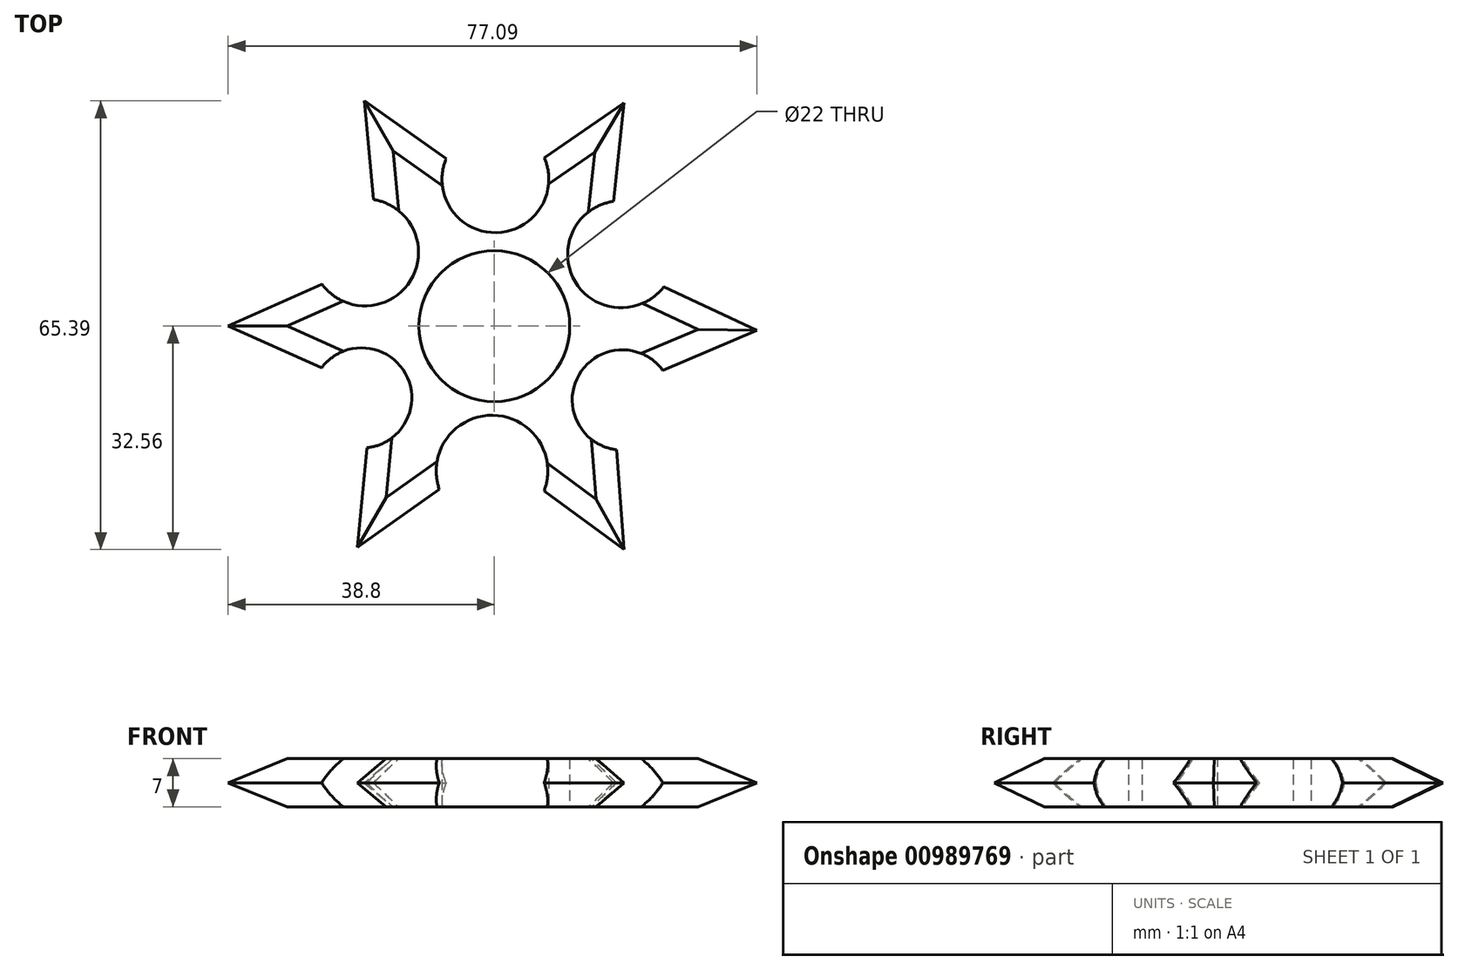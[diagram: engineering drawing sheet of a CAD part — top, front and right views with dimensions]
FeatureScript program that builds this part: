
annotation { "Feature Type Name" : "Feature", "Feature Type Description" : "" }
export const myFeature = defineFeature(function(context is Context, id is Id, definition is map)
    precondition{}
    {
        {
            var Q0;
            Q0=qCreatedBy(makeId("Top.planeOp"),FACE);
            var sketch = newSketch(context, id + "F0", { "sketchPlane" : qUnion([Q0])});
            skCircle(sketch, "E0", {"center": v(0, 0) * mm, "radius": 11 * mm});
            skPoint(sketch, "E1.start.orphan", {"position": v(-11, 0) * mm});
            skPoint(sketch, "E2.start.orphan", {"position": v(11, 0) * mm});
            skPoint(sketch, "E3", {"position": v(-5.5, 9.53) * mm});
            skPoint(sketch, "E4", {"position": v(5.64, 9.44) * mm});
            skPoint(sketch, "E5.MirrorCS.end.orphan", {"position": v(-39.57, 0) * mm});
            skPoint(sketch, "E6", {"position": v(-12.4, 21.5) * mm});
            skPoint(sketch, "E7", {"position": v(12.73, 21.31) * mm});
            skPoint(sketch, "E8", {"position": v(25.78, 0) * mm});
            skPoint(sketch, "E9", {"position": v(12.73, -21.31) * mm});
            skPoint(sketch, "E10", {"position": v(-13.4, -20.93) * mm});
            skPoint(sketch, "E11", {"position": v(-25.28, 0) * mm});
            skLineSegment(sketch, "E12", {"start": v(-17.92, 18.5) * mm, "end": v(-19.3, 33.48) * mm});
            skLineSegment(sketch, "E13", {"start": v(-6.9, 24.67) * mm, "end": v(-19.3, 33.48) * mm});
            skLineSegment(sketch, "E14", {"start": v(-39.57, 0) * mm, "end": v(-25.35, -6.32) * mm});
            skLineSegment(sketch, "E15", {"start": v(-25.28, 6.35) * mm, "end": v(-39.57, 0) * mm});
            skLineSegment(sketch, "E16", {"start": v(-18.9, -17.76) * mm, "end": v(-20.3, -32.9) * mm});
            skLineSegment(sketch, "E17", {"start": v(-7.9, -24.1) * mm, "end": v(-20.3, -32.9) * mm});
            skPoint(sketch, "E18.MirrorCS.start.orphan", {"position": v(-6.49, -8.96) * mm});
            skPoint(sketch, "E19", {"position": v(-18.84, 10.75) * mm});
            skPoint(sketch, "E20", {"position": v(-19.34, -10.47) * mm});
            skArc(sketch, "E21", {"start": v(-25.28, 6.35) * mm, "mid": v(-12.17, 6.7) * mm, "end": v(-17.92, 18.5) * mm});
            skArc(sketch, "E22", {"start": v(-18.9, -17.76) * mm, "mid": v(-12.98, -6.87) * mm, "end": v(-25.35, -6.32) * mm});
            skLineSegment(sketch, "E23", {"start": v(19.25, -33.17) * mm, "end": v(19.29, -33.17) * mm});
            skLineSegment(sketch, "E24.MirrorCS", {"start": v(7.15, 24.83) * mm, "end": v(19.3, 33.18) * mm});
            skLineSegment(sketch, "E25.MirrorCS", {"start": v(17.7, 18.23) * mm, "end": v(19.3, 33.18) * mm});
            skArc(sketch, "E26.MirrorCS", {"start": v(24.87, 5.97) * mm, "mid": v(11.77, 6.52) * mm, "end": v(17.7, 18.23) * mm});
            skLineSegment(sketch, "E27.MirrorCS", {"start": v(24.87, 5.97) * mm, "end": v(39.06, -0.6) * mm});
            skLineSegment(sketch, "E28.MirrorCS", {"start": v(39.06, -0.6) * mm, "end": v(24.75, -6.7) * mm});
            skLineSegment(sketch, "E29.MirrorCS", {"start": v(18.11, -18.04) * mm, "end": v(19.29, -33.2) * mm});
            skLineSegment(sketch, "E30.MirrorCS", {"start": v(7.14, -24.3) * mm, "end": v(19.29, -33.2) * mm});
            skArc(sketch, "E31.MirrorCS", {"start": v(18.11, -18.04) * mm, "mid": v(12.36, -7.07) * mm, "end": v(24.75, -6.7) * mm});
            skPoint(sketch, "E32.positionSnap0", {"position": v(0.16, 21.4) * mm});
            skPoint(sketch, "E33", {"position": v(-0.33, -21.12) * mm});
            skArc(sketch, "E34", {"start": v(-7.9, -24.1) * mm, "mid": v(-0.22, -13) * mm, "end": v(7.14, -24.3) * mm});
            skArc(sketch, "E35", {"start": v(-6.9, 24.67) * mm, "mid": v(0.25, 13.62) * mm, "end": v(7.15, 24.83) * mm});
            skPoint(sketch, "E36.MirrorCS.start.orphan", {"position": v(5.64, -9.44) * mm});
            skSolve(sketch);
        }
        {
            var Q0;
            Q0=makeQuery(id+"F0.imprint","IMPRINT",FACE,{"disambiguationData":[TD([[makeQuery(id+"F0.imprint","IMPRINT",EDGE,{"derivedFrom":sQuery(id+"F0.wireOp",EDGE,"E0")}),-1.0]])]});
            extrude(context, id + "F1", {"entities" : qUnion([Q0]), "depth" : 7 * mm, "offsetDistance" : 25.4 * mm});
        }
        {
            var Q0;
            Q0=makeQuery(id+"F1.opExtrude","CAP_EDGE",EDGE,{"disambiguationData":[OSD([sQuery(id+"F0.wireOp",EDGE,"E25.MirrorCS")])],"isStart":false});
            var Q1;
            Q1=makeQuery(id+"F1.opExtrude","CAP_EDGE",EDGE,{"disambiguationData":[OSD([sQuery(id+"F0.wireOp",EDGE,"E24.MirrorCS")])],"isStart":false});
            chamfer(context, id + "F2", {"entities" : qUnion([Q0, Q1]), "width" : 3.8 * mm, "tangentPropagation" : true});
        }
        {
            var Q0;
            Q0=makeQuery(id+"F1.opExtrude","CAP_EDGE",EDGE,{"disambiguationData":[OSD([sQuery(id+"F0.wireOp",EDGE,"E25.MirrorCS")])],"isStart":true});
            var Q1;
            Q1=makeQuery(id+"F1.opExtrude","CAP_EDGE",EDGE,{"disambiguationData":[OSD([sQuery(id+"F0.wireOp",EDGE,"E24.MirrorCS")])],"isStart":true});
            chamfer(context, id + "F3", {"entities" : qUnion([Q0, Q1]), "width" : 3.8 * mm, "tangentPropagation" : true});
        }
        {
            var Q0;
            Q0=makeQuery(id+"F1.opExtrude","CAP_EDGE",EDGE,{"disambiguationData":[OSD([sQuery(id+"F0.wireOp",EDGE,"E28.MirrorCS")])],"isStart":false});
            var Q1;
            Q1=makeQuery(id+"F1.opExtrude","CAP_EDGE",EDGE,{"disambiguationData":[OSD([sQuery(id+"F0.wireOp",EDGE,"E27.MirrorCS")])],"isStart":false});
            var Q2;
            Q2=makeQuery(id+"F1.opExtrude","CAP_EDGE",EDGE,{"disambiguationData":[OSD([sQuery(id+"F0.wireOp",EDGE,"E29.MirrorCS")])],"isStart":false});
            var Q3;
            Q3=makeQuery(id+"F1.opExtrude","CAP_EDGE",EDGE,{"disambiguationData":[OSD([sQuery(id+"F0.wireOp",EDGE,"E30.MirrorCS")])],"isStart":false});
            var Q4;
            Q4=makeQuery(id+"F1.opExtrude","CAP_EDGE",EDGE,{"disambiguationData":[OSD([sQuery(id+"F0.wireOp",EDGE,"E17")])],"isStart":false});
            var Q5;
            Q5=makeQuery(id+"F1.opExtrude","CAP_EDGE",EDGE,{"disambiguationData":[OSD([sQuery(id+"F0.wireOp",EDGE,"E16")])],"isStart":false});
            var Q6;
            Q6=makeQuery(id+"F1.opExtrude","CAP_EDGE",EDGE,{"disambiguationData":[OSD([sQuery(id+"F0.wireOp",EDGE,"E14")])],"isStart":false});
            var Q7;
            Q7=makeQuery(id+"F1.opExtrude","CAP_EDGE",EDGE,{"disambiguationData":[OSD([sQuery(id+"F0.wireOp",EDGE,"E15")])],"isStart":false});
            var Q8;
            Q8=makeQuery(id+"F1.opExtrude","CAP_EDGE",EDGE,{"disambiguationData":[OSD([sQuery(id+"F0.wireOp",EDGE,"E12")])],"isStart":false});
            var Q9;
            Q9=makeQuery(id+"F1.opExtrude","CAP_EDGE",EDGE,{"disambiguationData":[OSD([sQuery(id+"F0.wireOp",EDGE,"E13")])],"isStart":false});
            chamfer(context, id + "F4", {"entities" : qUnion([Q0, Q1, Q2, Q3, Q4, Q5, Q6, Q7, Q8, Q9]), "width" : 3.8 * mm, "tangentPropagation" : true});
        }
        {
            var Q0;
            Q0=makeQuery(id+"F1.opExtrude","CAP_EDGE",EDGE,{"disambiguationData":[OSD([sQuery(id+"F0.wireOp",EDGE,"E27.MirrorCS")])],"isStart":true});
            var Q1;
            Q1=makeQuery(id+"F1.opExtrude","CAP_EDGE",EDGE,{"disambiguationData":[OSD([sQuery(id+"F0.wireOp",EDGE,"E28.MirrorCS")])],"isStart":true});
            var Q2;
            Q2=makeQuery(id+"F1.opExtrude","CAP_EDGE",EDGE,{"disambiguationData":[OSD([sQuery(id+"F0.wireOp",EDGE,"E17")])],"isStart":true});
            var Q3;
            Q3=makeQuery(id+"F1.opExtrude","CAP_EDGE",EDGE,{"disambiguationData":[OSD([sQuery(id+"F0.wireOp",EDGE,"E16")])],"isStart":true});
            var Q4;
            Q4=makeQuery(id+"F1.opExtrude","CAP_EDGE",EDGE,{"disambiguationData":[OSD([sQuery(id+"F0.wireOp",EDGE,"E30.MirrorCS")])],"isStart":true});
            var Q5;
            Q5=makeQuery(id+"F1.opExtrude","CAP_EDGE",EDGE,{"disambiguationData":[OSD([sQuery(id+"F0.wireOp",EDGE,"E14")])],"isStart":true});
            var Q6;
            Q6=makeQuery(id+"F1.opExtrude","CAP_EDGE",EDGE,{"disambiguationData":[OSD([sQuery(id+"F0.wireOp",EDGE,"E15")])],"isStart":true});
            var Q7;
            Q7=makeQuery(id+"F1.opExtrude","CAP_EDGE",EDGE,{"disambiguationData":[OSD([sQuery(id+"F0.wireOp",EDGE,"E12")])],"isStart":true});
            var Q8;
            Q8=makeQuery(id+"F1.opExtrude","CAP_EDGE",EDGE,{"disambiguationData":[OSD([sQuery(id+"F0.wireOp",EDGE,"E13")])],"isStart":true});
            chamfer(context, id + "F5", {"entities" : qUnion([Q0, Q1, Q2, Q3, Q4, Q5, Q6, Q7, Q8]), "width" : 3.8 * mm, "tangentPropagation" : true});
        }
        {
            var Q0;
            Q0=makeQuery(id+"F1.opExtrude","CAP_EDGE",EDGE,{"disambiguationData":[OSD([sQuery(id+"F0.wireOp",EDGE,"E29.MirrorCS")])],"isStart":true});
            chamfer(context, id + "F6", {"entities" : qUnion([Q0]), "width" : 3.8 * mm, "tangentPropagation" : true});
        }
    });
